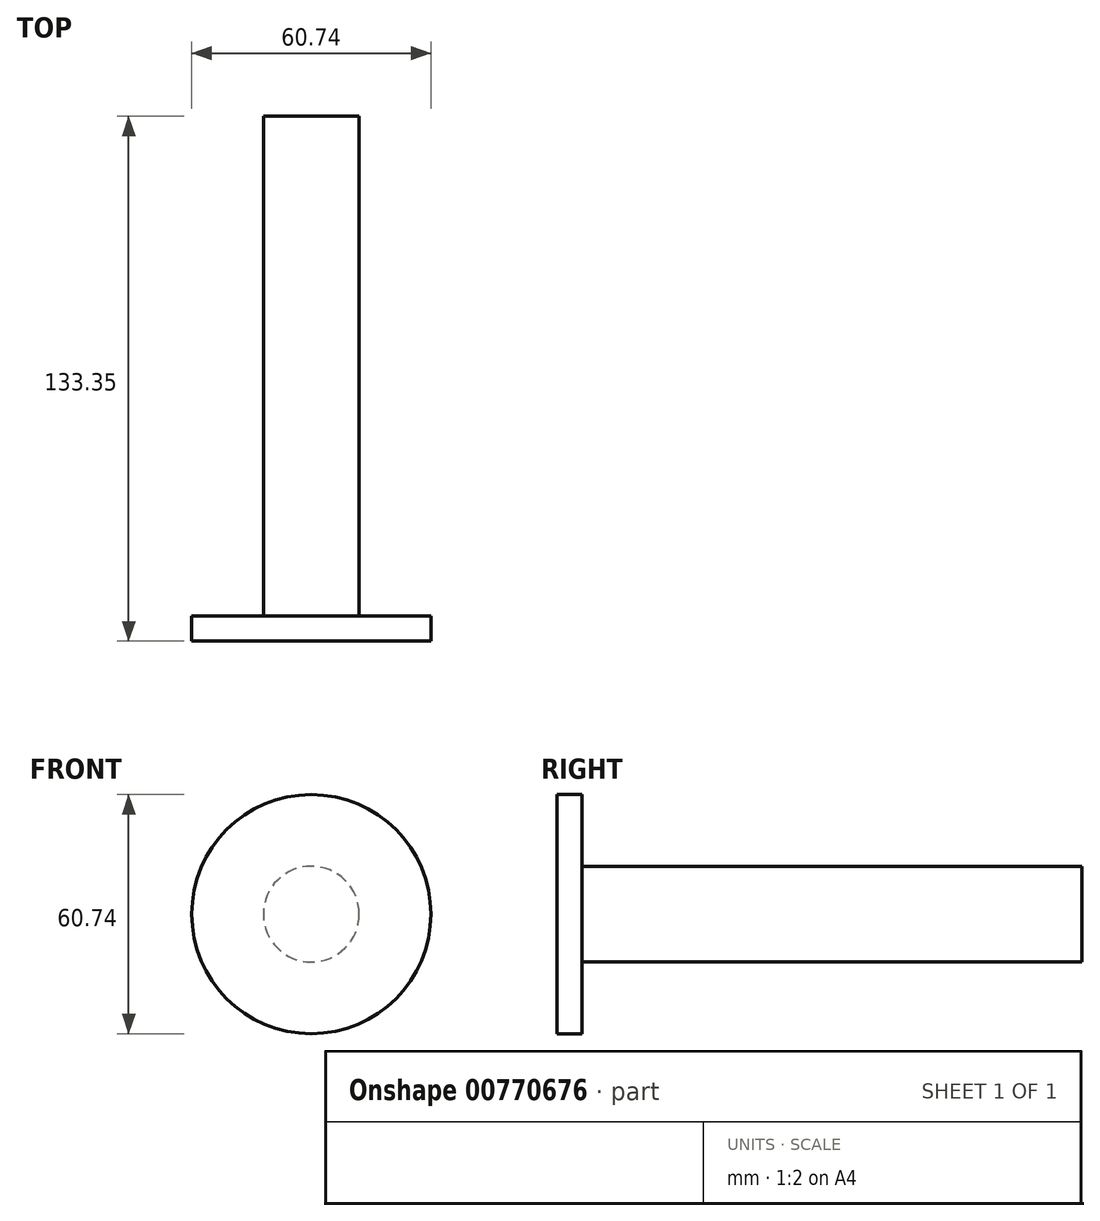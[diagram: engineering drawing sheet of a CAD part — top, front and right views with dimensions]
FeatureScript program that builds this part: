
annotation { "Feature Type Name" : "Feature", "Feature Type Description" : "" }
export const myFeature = defineFeature(function(context is Context, id is Id, definition is map)
    precondition{}
    {
        {
            var Q0;
            Q0=qCreatedBy(makeId("Front.planeOp"),FACE);
            var sketch = newSketch(context, id + "F0", { "sketchPlane" : qUnion([Q0])});
            skCircle(sketch, "E0", {"center": v(0, 0) * mm, "radius": 12.17 * mm});
            skCircle(sketch, "E1", {"center": v(0, 0) * mm, "radius": 43.1 * mm});
            skSolve(sketch);
        }
        {
            var Q0;
            Q0=makeQuery(id+"F0.imprint","IMPRINT",FACE,{"disambiguationData":[TD([[makeQuery(id+"F0.imprint","IMPRINT",EDGE,{"derivedFrom":sQuery(id+"F0.wireOp",EDGE,"E0")}),1.0]])]});
            var Q1;
            Q1=sQuery(id+"F0.wireOp",EDGE,"E0");
            extrude(context, id + "F1", {"entities" : qUnion([Q0]), "surfaceEntities" : qUnion([Q1]), "depth" : 127 * mm, "offsetDistance" : 25.4 * mm});
        }
        {
            var Q0;
            Q0=makeQuery(id+"F1.opExtrude","CAP_FACE",FACE,{"disambiguationData":[OSD([sQuery(id+"F0.wireOp",EDGE,"E0")])],"isStart":false});
            var sketch = newSketch(context, id + "F2", { "sketchPlane" : qUnion([Q0])});
            skCircle(sketch, "E2", {"center": v(0, 0) * mm, "radius": 30.37 * mm});
            skSolve(sketch);
        }
        {
            var Q0;
            Q0=makeQuery(id+"F2.imprint","IMPRINT",FACE,{"disambiguationData":[TD([[makeQuery(id+"F2.imprint","IMPRINT",EDGE,{"derivedFrom":sQuery(id+"F2.wireOp",EDGE,"E2")}),1.0]])]});
            var Q1;
            Q1=makeQuery(id+"F2.imprint","IMPRINT",FACE,{"disambiguationData":[TD([[makeQuery(id+"F2.imprint","IMPRINT",EDGE,{"derivedFrom":makeQuery(id+"F1.opExtrude","CAP_EDGE",EDGE,{"disambiguationData":[OSD([sQuery(id+"F0.wireOp",EDGE,"E0")])],"isStart":false})}),1.0]])]});
            extrude(context, id + "F3", {"entities" : qUnion([Q0, Q1]), "operationType" : NewBodyOperationType.ADD, "depth" : 6.35 * mm, "offsetDistance" : 25.4 * mm});
        }
    });
